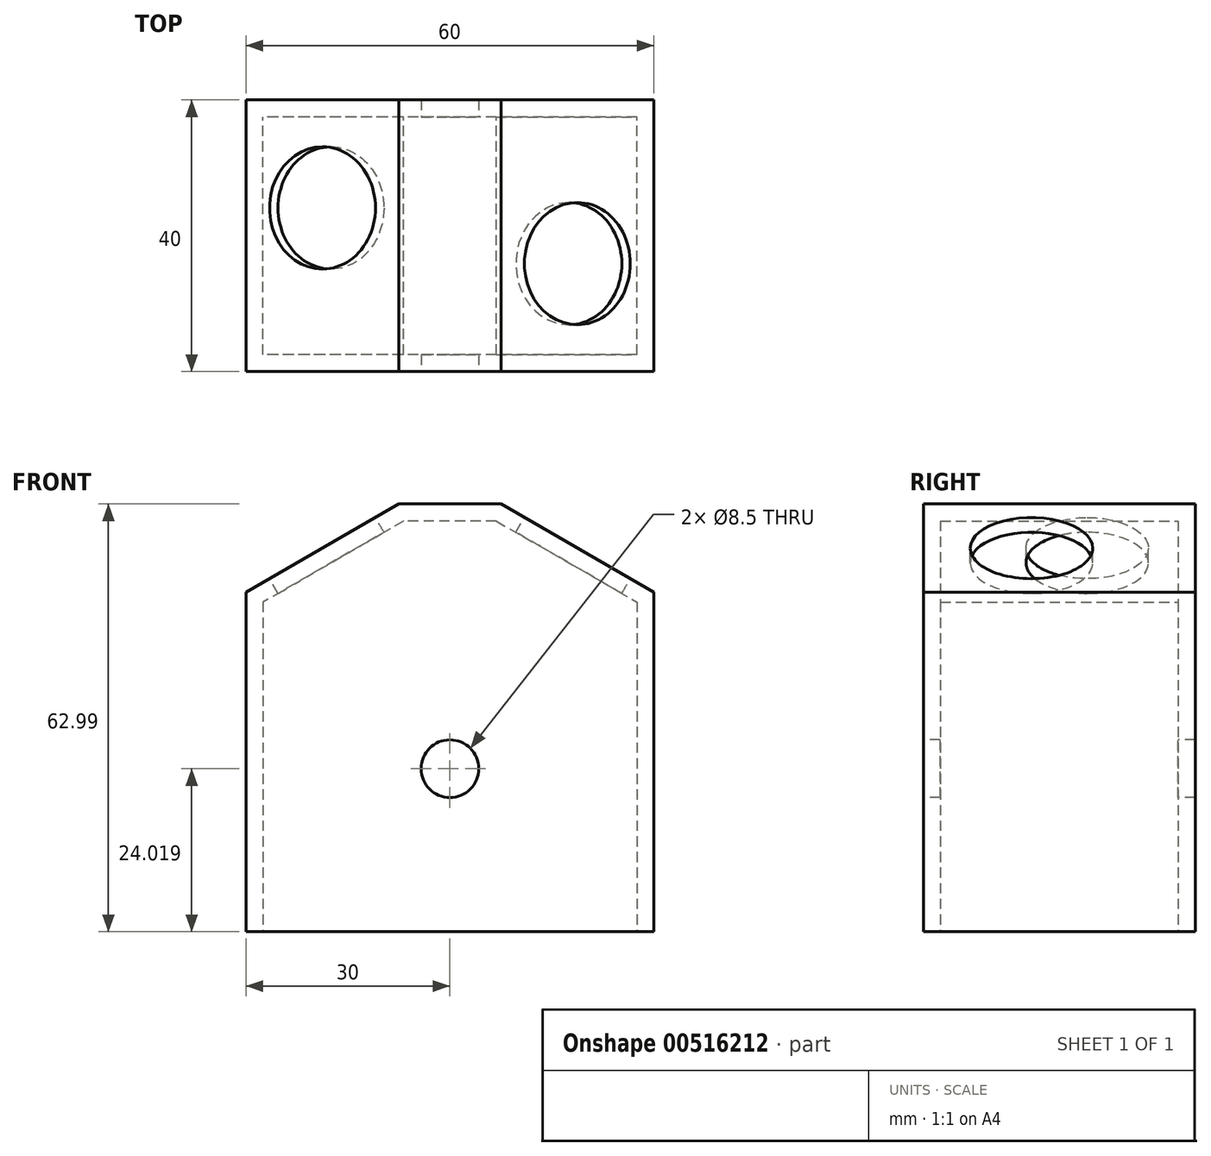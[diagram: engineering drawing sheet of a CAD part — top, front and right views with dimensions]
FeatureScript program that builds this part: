
annotation { "Feature Type Name" : "Feature", "Feature Type Description" : "" }
export const myFeature = defineFeature(function(context is Context, id is Id, definition is map)
    precondition{}
    {
        {
            var Q0;
            Q0=qCreatedBy(makeId("Front.planeOp"),FACE);
            var sketch = newSketch(context, id + "F0", { "sketchPlane" : qUnion([Q0])});
            skLineSegment(sketch, "E0.bottom", {"start": v(30, 25) * mm, "end": v(-30, 25) * mm});
            skLineSegment(sketch, "E0.top", {"start": v(30, -25) * mm, "end": v(-30, -25) * mm});
            skLineSegment(sketch, "E0.left", {"start": v(30, 25) * mm, "end": v(30, -25) * mm});
            skLineSegment(sketch, "E0.right", {"start": v(-30, 25) * mm, "end": v(-30, -25) * mm});
            skPoint(sketch, "E0.middle", {"position": v(0, 0) * mm});
            skPoint(sketch, "E1.endSnap0", {"position": v(0, 25) * mm});
            skLineSegment(sketch, "E2.bottom", {"start": v(7.5, 38) * mm, "end": v(-7.5, 38) * mm});
            skLineSegment(sketch, "E2.left", {"start": v(7.5, 38) * mm, "end": v(7.5, 25) * mm});
            skLineSegment(sketch, "E2.right", {"start": v(-7.5, 38) * mm, "end": v(-7.5, 25) * mm});
            skPoint(sketch, "E3", {"position": v(0, 38) * mm});
            skLineSegment(sketch, "E4", {"start": v(-7.5, 38) * mm, "end": v(-30, 25) * mm});
            skLineSegment(sketch, "E5", {"start": v(7.5, 38) * mm, "end": v(30, 25) * mm});
            skLineSegment(sketch, "E6", {"start": v(18.75, 31.5) * mm, "end": v(0, -0.98) * mm});
            skLineSegment(sketch, "E7", {"start": v(-18.75, 31.5) * mm, "end": v(0, -0.98) * mm});
            skPoint(sketch, "E8", {"position": v(0, -0.98) * mm});
            skSolve(sketch);
        }
        {
            var Q0;
            Q0=makeQuery(id+"F0.imprint","IMPRINT",FACE,{"disambiguationData":[TD([[makeQuery(id+"F0.imprint","IMPRINT",EDGE,{"derivedFrom":sQuery(id+"F0.wireOp",EDGE,"E0.top")}),-1.0]])]});
            var Q1;
            {var subQ2=sQuery(id+"F0.wireOp",EDGE,"E2.left");Q1=makeQuery(id+"F0.imprint","IMPRINT",FACE,{"disambiguationData":[TD([[makeQuery(id+"F0.imprint","IMPRINT",EDGE,{"derivedFrom":subQ2}),1.0]])]});}
            var Q2;
            Q2=makeQuery(id+"F0.imprint","IMPRINT",FACE,{"disambiguationData":[TD([[makeQuery(id+"F0.imprint","IMPRINT",EDGE,{"derivedFrom":sQuery(id+"F0.wireOp",EDGE,"E2.bottom")}),1.0]])]});
            var Q3;
            {var subQ2=sQuery(id+"F0.wireOp",EDGE,"E2.right");Q3=makeQuery(id+"F0.imprint","IMPRINT",FACE,{"disambiguationData":[TD([[makeQuery(id+"F0.imprint","IMPRINT",EDGE,{"derivedFrom":subQ2}),-1.0]])]});}
            var Q4;
            {var subQ0=sQuery(id+"F0.wireOp",EDGE,"E4");var subQ3=sQuery(id+"F0.wireOp",EDGE,"E7");var subQ5=makeQuery(id+"F0.imprint","INTERSECT",VERTEX,{"derivedFrom":[subQ0,subQ3]});Q4=makeQuery(id+"F0.imprint","IMPRINT",FACE,{"disambiguationData":[TD([[makeQuery(id+"F0.imprint","IMPRINT",EDGE,{"disambiguationData":[TD([[subQ5,-1.0]])],"derivedFrom":subQ3}),-1.0]])]});}
            var Q5;
            {var subQ0=sQuery(id+"F0.wireOp",EDGE,"E5");var subQ3=sQuery(id+"F0.wireOp",EDGE,"E6");var subQ5=makeQuery(id+"F0.imprint","INTERSECT",VERTEX,{"derivedFrom":[subQ0,subQ3]});Q5=makeQuery(id+"F0.imprint","IMPRINT",FACE,{"disambiguationData":[TD([[makeQuery(id+"F0.imprint","IMPRINT",EDGE,{"disambiguationData":[TD([[subQ5,-1.0]])],"derivedFrom":subQ3}),1.0]])]});}
            var Q6;
            {var subQ0=sQuery(id+"F0.wireOp",EDGE,"E0.bottom");var subQ4=makeQuery(id+"F0.imprint","INTERSECT",VERTEX,{"derivedFrom":[subQ0,sQuery(id+"F0.wireOp",EDGE,"E2.left")]});Q6=makeQuery(id+"F0.imprint","IMPRINT",FACE,{"disambiguationData":[TD([[makeQuery(id+"F0.imprint","IMPRINT",EDGE,{"disambiguationData":[TD([[subQ4,1.0]])],"derivedFrom":subQ0}),1.0]])]});}
            extrude(context, id + "F1", {"entities" : qUnion([Q0, Q1, Q2, Q3, Q4, Q5, Q6]), "depth" : 40 * mm, "offsetDistance" : 25 * mm});
        }
        {
            var Q0;
            Q0=makeQuery(id+"F1.opExtrude","SWEPT_FACE",FACE,{"disambiguationData":[OSD([sQuery(id+"F0.wireOp",EDGE,"E4")])]});
            var sketch = newSketch(context, id + "F2", { "sketchPlane" : qUnion([Q0])});
            skLineSegment(sketch, "E9", {"start": v(-0.5, 0) * mm, "end": v(-0.5, -15.9) * mm});
            skPoint(sketch, "E9.endSnap0", {"position": v(-0.5, 0) * mm});
            skCircle(sketch, "E10", {"center": v(-0.5, -15.9) * mm, "radius": 9 * mm});
            skSolve(sketch);
        }
        {
            var Q0;
            Q0=makeQuery(id+"F1.opExtrude","SWEPT_FACE",FACE,{"disambiguationData":[OSD([sQuery(id+"F0.wireOp",EDGE,"E5")])]});
            var sketch = newSketch(context, id + "F3", { "sketchPlane" : qUnion([Q0])});
            skLineSegment(sketch, "E11", {"start": v(0.5, -40) * mm, "end": v(0.5, -24.1) * mm});
            skCircle(sketch, "E12", {"center": v(0.5, -24.1) * mm, "radius": 9 * mm});
            skSolve(sketch);
        }
        {
            var Q0;
            Q0=makeQuery(id+"F1.opExtrude","SWEPT_FACE",FACE,{"disambiguationData":[OSD([sQuery(id+"F0.wireOp",EDGE,"E0.top")])]});
            shell(context, id + "F4", {"entities" : qUnion([Q0]), "thickness" : 2.5 * mm});
        }
        {
            var Q0;
            Q0=makeQuery(id+"F3.imprint","IMPRINT",FACE,{"disambiguationData":[TD([[makeQuery(id+"F3.imprint","IMPRINT",EDGE,{"derivedFrom":sQuery(id+"F3.wireOp",EDGE,"E12")}),1.0]])]});
            extrude(context, id + "F5", {"entities" : qUnion([Q0]), "operationType" : NewBodyOperationType.REMOVE, "oppositeDirection" : true, "depth" : 25 * mm, "offsetDistance" : 25 * mm});
        }
        {
            var Q0;
            Q0=makeQuery(id+"F2.imprint","IMPRINT",FACE,{"disambiguationData":[TD([[makeQuery(id+"F2.imprint","IMPRINT",EDGE,{"derivedFrom":sQuery(id+"F2.wireOp",EDGE,"E10")}),1.0]])]});
            extrude(context, id + "F6", {"entities" : qUnion([Q0]), "operationType" : NewBodyOperationType.REMOVE, "oppositeDirection" : true, "depth" : 25 * mm, "offsetDistance" : 25 * mm});
        }
        {
            var Q0;
            Q0=makeQuery(id+"F1.opExtrude","CAP_FACE",FACE,{"disambiguationData":[OSD([sQuery(id+"F0.wireOp",EDGE,"E0.top"),sQuery(id+"F0.wireOp",EDGE,"E0.left"),sQuery(id+"F0.wireOp",EDGE,"E0.right"),sQuery(id+"F0.wireOp",EDGE,"E2.bottom"),sQuery(id+"F0.wireOp",EDGE,"E4"),sQuery(id+"F0.wireOp",EDGE,"E5")])],"isStart":false});
            var sketch = newSketch(context, id + "F7", { "sketchPlane" : qUnion([Q0])});
            skCircle(sketch, "E13", {"center": v(0, -0.98) * mm, "radius": 4.25 * mm});
            skSolve(sketch);
        }
        {
            var Q0;
            Q0=makeQuery(id+"F7.imprint","IMPRINT",FACE,{"disambiguationData":[TD([[makeQuery(id+"F7.imprint","IMPRINT",EDGE,{"derivedFrom":sQuery(id+"F7.wireOp",EDGE,"E13")}),1.0]])]});
            extrude(context, id + "F8", {"entities" : qUnion([Q0]), "operationType" : NewBodyOperationType.REMOVE, "oppositeDirection" : true, "depth" : 40 * mm, "offsetDistance" : 25 * mm});
        }
    });
